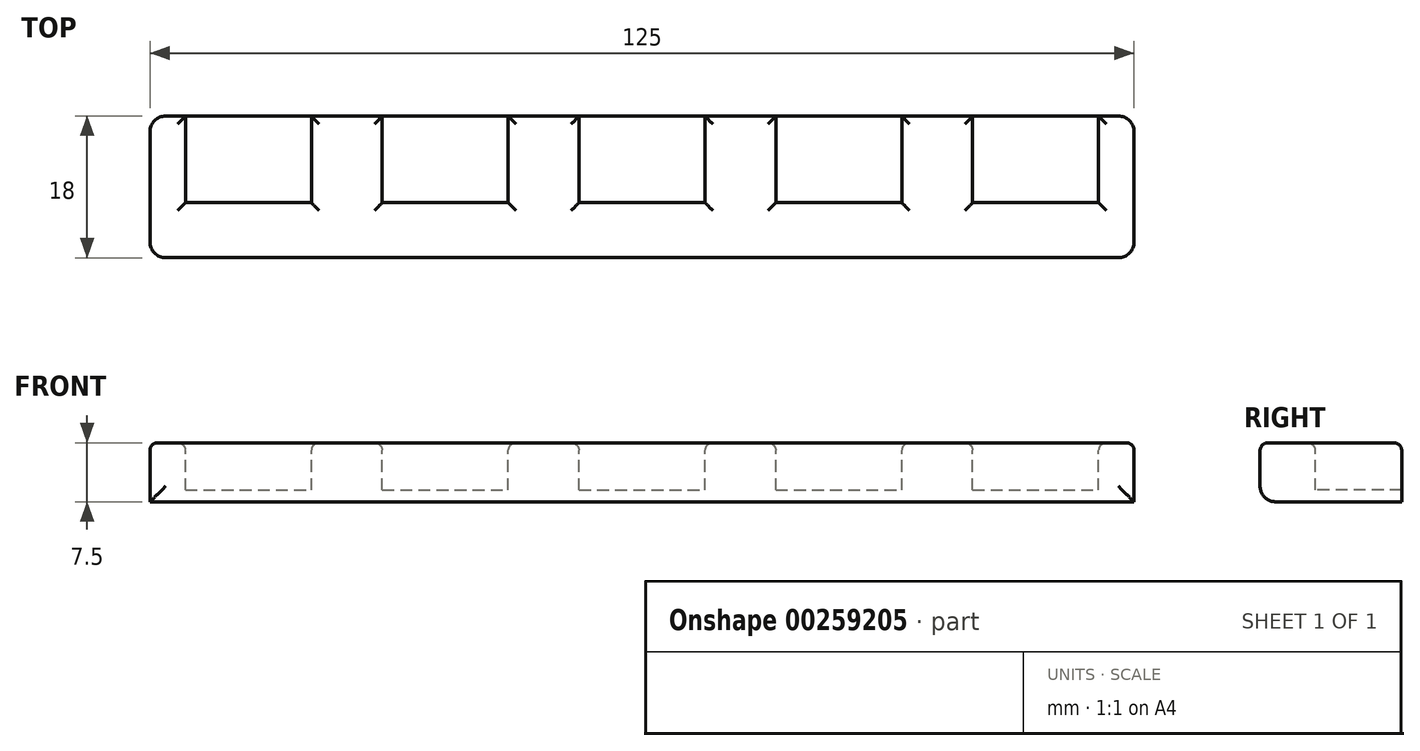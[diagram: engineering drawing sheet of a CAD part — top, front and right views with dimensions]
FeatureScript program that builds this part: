
annotation { "Feature Type Name" : "Feature", "Feature Type Description" : "" }
export const myFeature = defineFeature(function(context is Context, id is Id, definition is map)
    precondition{}
    {
        {
            var Q0;
            Q0=qCreatedBy(makeId("Top.planeOp"),FACE);
            var sketch = newSketch(context, id + "F0", { "sketchPlane" : qUnion([Q0])});
            skLineSegment(sketch, "E0.bottom", {"start": v(-64.97, 25.13) * mm, "end": v(60.03, 25.13) * mm});
            skLineSegment(sketch, "E0.top", {"start": v(-64.97, 7.13) * mm, "end": v(60.03, 7.13) * mm});
            skLineSegment(sketch, "E0.left", {"start": v(-64.97, 25.13) * mm, "end": v(-64.97, 7.13) * mm});
            skLineSegment(sketch, "E0.right", {"start": v(60.03, 25.13) * mm, "end": v(60.03, 7.13) * mm});
            skSolve(sketch);
        }
        {
            var Q0;
            Q0 = qSketchRegion(id + "F0", true);
            extrude(context, id + "F1", {"entities" : qUnion([Q0]), "oppositeDirection" : true, "depth" : 7.5 * mm});
        }
        {
            var Q0;
            Q0=qCreatedBy(makeId("Top.planeOp"),FACE);
            var sketch = newSketch(context, id + "F2", { "sketchPlane" : qUnion([Q0])});
            skLineSegment(sketch, "E1.bottom", {"start": v(-60.47, 25.13) * mm, "end": v(-44.47, 25.13) * mm});
            skLineSegment(sketch, "E1.top", {"start": v(-60.47, 14.13) * mm, "end": v(-44.47, 14.13) * mm});
            skLineSegment(sketch, "E1.left", {"start": v(-60.47, 25.13) * mm, "end": v(-60.47, 14.13) * mm});
            skLineSegment(sketch, "E1.right", {"start": v(-44.47, 25.13) * mm, "end": v(-44.47, 14.13) * mm});
            skLineSegment(sketch, "E2.1.0.0", {"start": v(-35.47, 14.13) * mm, "end": v(-19.47, 14.13) * mm});
            skLineSegment(sketch, "E2.1.0.1", {"start": v(-35.47, 25.13) * mm, "end": v(-35.47, 14.13) * mm});
            skLineSegment(sketch, "E2.1.0.2", {"start": v(-35.47, 25.13) * mm, "end": v(-19.47, 25.13) * mm});
            skLineSegment(sketch, "E2.1.0.3", {"start": v(-19.47, 25.13) * mm, "end": v(-19.47, 14.13) * mm});
            skLineSegment(sketch, "E2.2.0.0", {"start": v(-10.47, 14.13) * mm, "end": v(5.53, 14.13) * mm});
            skLineSegment(sketch, "E2.2.0.1", {"start": v(-10.47, 25.13) * mm, "end": v(-10.47, 14.13) * mm});
            skLineSegment(sketch, "E2.2.0.2", {"start": v(-10.47, 25.13) * mm, "end": v(5.53, 25.13) * mm});
            skLineSegment(sketch, "E2.2.0.3", {"start": v(5.53, 25.13) * mm, "end": v(5.53, 14.13) * mm});
            skLineSegment(sketch, "E2.3.0.0", {"start": v(14.53, 14.13) * mm, "end": v(30.53, 14.13) * mm});
            skLineSegment(sketch, "E2.3.0.1", {"start": v(14.53, 25.13) * mm, "end": v(14.53, 14.13) * mm});
            skLineSegment(sketch, "E2.3.0.2", {"start": v(14.53, 25.13) * mm, "end": v(30.53, 25.13) * mm});
            skLineSegment(sketch, "E2.3.0.3", {"start": v(30.53, 25.13) * mm, "end": v(30.53, 14.13) * mm});
            skLineSegment(sketch, "E2.4.0.0", {"start": v(39.53, 14.13) * mm, "end": v(55.53, 14.13) * mm});
            skLineSegment(sketch, "E2.4.0.1", {"start": v(39.53, 25.13) * mm, "end": v(39.53, 14.13) * mm});
            skLineSegment(sketch, "E2.4.0.2", {"start": v(39.53, 25.13) * mm, "end": v(55.53, 25.13) * mm});
            skLineSegment(sketch, "E2.4.0.3", {"start": v(55.53, 25.13) * mm, "end": v(55.53, 14.13) * mm});
            skLineSegment(sketch, "E2.direction1", {"start": v(-60.47, 14.13) * mm, "end": v(-35.47, 14.13) * mm, "construction": true});
            skSolve(sketch);
        }
        {
            var Q0;
            Q0 = qSketchRegion(id + "F2", true);
            extrude(context, id + "F3", {"entities" : qUnion([Q0]), "operationType" : NewBodyOperationType.REMOVE, "oppositeDirection" : true, "depth" : 6 * mm});
        }
        {
            var Q0;
            Q0=makeQuery(id+"F1.opExtrude","SWEPT_EDGE",EDGE,{"disambiguationData":[OSD([sQuery(id+"F0.wireOp",EDGE,"E0.bottom"),sQuery(id+"F0.wireOp",EDGE,"E0.right")])]});
            var Q1;
            Q1=makeQuery(id+"F1.opExtrude","SWEPT_EDGE",EDGE,{"disambiguationData":[OSD([sQuery(id+"F0.wireOp",EDGE,"E0.top"),sQuery(id+"F0.wireOp",EDGE,"E0.right")])]});
            var Q2;
            Q2=makeQuery(id+"F1.opExtrude","SWEPT_EDGE",EDGE,{"disambiguationData":[OSD([sQuery(id+"F0.wireOp",EDGE,"E0.bottom"),sQuery(id+"F0.wireOp",EDGE,"E0.left")])]});
            var Q3;
            Q3=makeQuery(id+"F1.opExtrude","SWEPT_EDGE",EDGE,{"disambiguationData":[OSD([sQuery(id+"F0.wireOp",EDGE,"E0.top"),sQuery(id+"F0.wireOp",EDGE,"E0.left")])]});
            var Q4;
            Q4=makeQuery(id+"F1.opExtrude","CAP_EDGE",EDGE,{"disambiguationData":[OSD([sQuery(id+"F0.wireOp",EDGE,"E0.top")])],"isStart":false});
            fillet(context, id + "F4", {"entities" : qUnion([Q0, Q1, Q2, Q3, Q4]), "radius" : 2 * mm, "tangentPropagation" : true, "allowEdgeOverflow" : false});
        }
        {
            var Q0;
            Q0=makeQuery(id+"F1.opExtrude","CAP_FACE",FACE,{"disambiguationData":[OSD([sQuery(id+"F0.wireOp",EDGE,"E0.bottom"),sQuery(id+"F0.wireOp",EDGE,"E0.top"),sQuery(id+"F0.wireOp",EDGE,"E0.left"),sQuery(id+"F0.wireOp",EDGE,"E0.right")])],"isStart":true});
            fillet(context, id + "F5", {"entities" : qUnion([Q0]), "radius" : 1 * mm, "tangentPropagation" : true, "allowEdgeOverflow" : false});
        }
    });
